# Revit family: NBS_Allermuir_DmstcChrs_Mote-en-us_Ottoman-MTEOT120
name_source: partatom
category: Furniture
revit_build: Autodesk Revit 2016 (Build: 20151007_0715(x64)
units: mm (PartAtom-declared; Revit-internal decimal feet)

## family parameters
Always vertical = Yes
Cut with Voids When Loaded = No
Room Calculation Point = No
Shared = No
Work Plane-Based = No

## types (1)
- MTEOT120
    AssetType = Moveable
    BIMObjectName = NBS_Allermuir_DomesticChairs_Mote_MTEOT120-US
    Category = Pr_40_50_12_22:Dining chairs
    Depth = 30 "
    Description = 120° ottoman
    DurationUnit = year
    ExpectedLife = 10
    Features = Fully upholstered, cast aluminum legs and aluminum perimeter frame finished in black powder coat, plastic glides with leveling adjustment, cast aluminum frame available in flint gray, mineral sand, mellow yellow or orange crush, 1 x front facing, frame integrated power unit - 2 x powered USB and 1 x power outlet, 1 x rear facing, frame integrated power unit - 2 x powered USB and 1 x power outlet, two-tone upholstery
    FrameColourOptions = Flint grey, mineral sand, mellow yellow, orange crush
    FrameHeight = 10 "
    FrameMountingMaterial = NBS_Concept
    FramesColour = Black
    FramesFinish = Powder coat
    FramesMaterial = Aluminium
    HighestSeatingHeight = 0 "
    IfcExportAs = IfcFurnitureType
    IfcExportType = SOFA
    IsBuiltIn = No
    LowestSeatingHeight = 0 "
    ManufacturerName = Allermuir
    ManufacturerURL = http://www.thesenatorgroup.com
    ModelNumber = MTE-OT120
    ModelReference = Mote ottoman
    NBSCertification = www.nationalbimlibrary.com/cert/ak1y1ojf
    NBSDescription = Domestic chairs
    NBSReference = 45-35-20/365
    Name = DomesticChairs_Mote_MTE-OT120_Allermuir
    NominalDepth = 80 "
    NominalHeight = 19 "
    NominalLength = 41 "
    NominalWidth = 80 "
    OmniClassCode = 22-12 52 23
    OmniClassTitle = Office Seating
    OmniClassVersion = Table 22 2012-05-16
    OptionalAccessories = 1 x front facing frame intergrated power unit with 2 x powered USB and 1 x power socket, 2 x rear facing frame intergrated power unit with 2 x powered USB and 1 x power socket
    ProductInformation = http://www.thesenatorgroup.com
    SeatAngle = 120.00°
    SeatEndRestOffset = 3 "
    SeatFrameMaterial = NBS_Concept
    SeatFrameWidth = 2 "
    SeatLegOffset = 6 "
    SeatOverallWidth = 80 "
    SeatPowerSupplyMaterial = NBS_Concept
    SeatingArmRestMaterial = NBS_Concept
    SeatingHeight = 19 "
    SeatingSeatMaterial = NBS_Concept
    SeatsAndBacksFinish = Two-tone upholstery available
    SeatsAndBacksMaterial = Upholstered
    Size = 40.5 x 80.25 x 18.5"
    Status = UNSET
    Uniclass2015Code = Pr_40_50_12_22
    Uniclass2015Title = Dining chairs
    Uniclass2015Version = Products v1.9
    Version = 1
    WarrantyDescription = Allermuir warrant that its manufactured products are free from manufacturing defects in materials or workmanship for a period of ten years
    WarrantyDurationParts = 10
    WarrantyDurationUnit = year

## geometry (parser evidence)
native form markers: Sweep x9
no freeform markers — native parametric forms only
